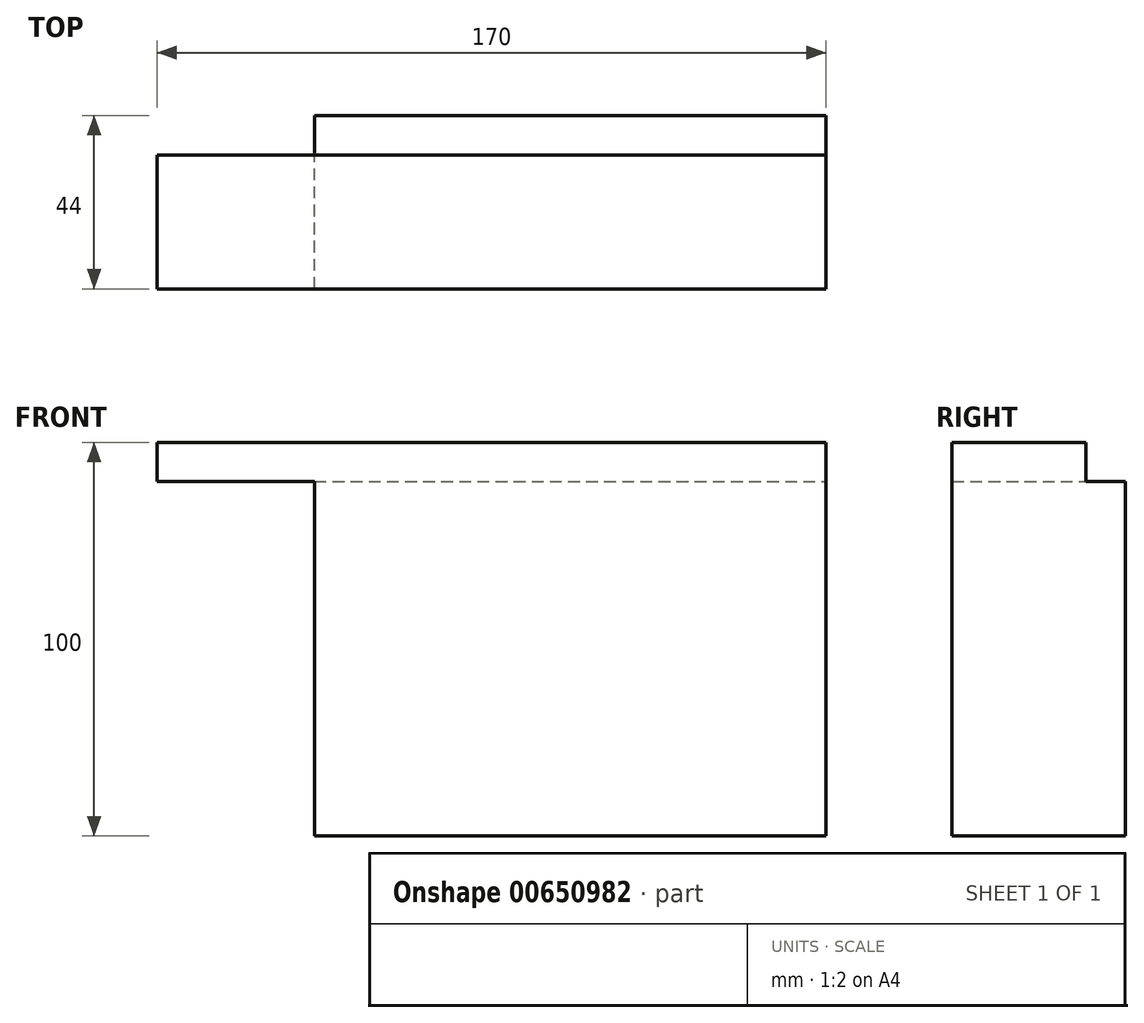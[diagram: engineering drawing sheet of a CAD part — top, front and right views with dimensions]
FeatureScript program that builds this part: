
annotation { "Feature Type Name" : "Feature", "Feature Type Description" : "" }
export const myFeature = defineFeature(function(context is Context, id is Id, definition is map)
    precondition{}
    {
        {
            var Q0;
            Q0=qCreatedBy(makeId("Top.planeOp"),FACE);
            var sketch = newSketch(context, id + "F0", { "sketchPlane" : qUnion([Q0])});
            skLineSegment(sketch, "E0.bottom", {"start": v(0, 0) * mm, "end": v(130, 0) * mm});
            skLineSegment(sketch, "E0.top", {"start": v(0, 44) * mm, "end": v(130, 44) * mm});
            skLineSegment(sketch, "E0.left", {"start": v(0, 0) * mm, "end": v(0, 44) * mm});
            skLineSegment(sketch, "E0.right", {"start": v(130, 0) * mm, "end": v(130, 44) * mm});
            skSolve(sketch);
        }
        {
            var Q0;
            Q0=makeQuery(id+"F0.imprint","IMPRINT",FACE,{"disambiguationData":[TD([[makeQuery(id+"F0.imprint","IMPRINT",EDGE,{"derivedFrom":sQuery(id+"F0.wireOp",EDGE,"E0.bottom")}),1.0]])]});
            extrude(context, id + "F1", {"entities" : qUnion([Q0]), "depth" : 90 * mm, "offsetDistance" : 25.4 * mm});
        }
        {
            var Q0;
            Q0=makeQuery(id+"F1.opExtrude","CAP_FACE",FACE,{"disambiguationData":[OSD([sQuery(id+"F0.wireOp",EDGE,"E0.bottom"),sQuery(id+"F0.wireOp",EDGE,"E0.top"),sQuery(id+"F0.wireOp",EDGE,"E0.left"),sQuery(id+"F0.wireOp",EDGE,"E0.right")])],"isStart":false});
            var sketch = newSketch(context, id + "F2", { "sketchPlane" : qUnion([Q0])});
            skLineSegment(sketch, "E1.bottom", {"start": v(130, 0) * mm, "end": v(-40, 0) * mm});
            skLineSegment(sketch, "E1.top", {"start": v(130, 34) * mm, "end": v(-40, 34) * mm});
            skLineSegment(sketch, "E1.left", {"start": v(130, 0) * mm, "end": v(130, 34) * mm});
            skLineSegment(sketch, "E1.right", {"start": v(-40, 0) * mm, "end": v(-40, 34) * mm});
            skSolve(sketch);
        }
        {
            var Q0;
            {var subQ3=sQuery(id+"F2.wireOp",EDGE,"E1.left");Q0=makeQuery(id+"F2.imprint","IMPRINT",FACE,{"disambiguationData":[TD([[makeQuery(id+"F2.imprint","IMPRINT",EDGE,{"derivedFrom":subQ3}),1.0]])]});}
            var Q1;
            {var subQ3=sQuery(id+"F2.wireOp",EDGE,"E1.right");Q1=makeQuery(id+"F2.imprint","IMPRINT",FACE,{"disambiguationData":[TD([[makeQuery(id+"F2.imprint","IMPRINT",EDGE,{"derivedFrom":subQ3}),-1.0]])]});}
            extrude(context, id + "F3", {"entities" : qUnion([Q0, Q1]), "operationType" : NewBodyOperationType.ADD, "depth" : 10 * mm, "offsetDistance" : 25.4 * mm});
        }
    });
